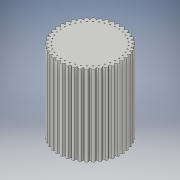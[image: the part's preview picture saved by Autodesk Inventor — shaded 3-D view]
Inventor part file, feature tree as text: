
AUTODESK INVENTOR PART (.ipt)
format: ipt  version: 2019.3 (Build 233278000, 278)  size: 697,856 bytes
history: native  units: mm
features: extrude x1
ambient origin geometry x8: Origin, YZ Plane, XZ Plane, XY Plane, X Axis, Y Axis, Z Axis, Center Point
bodies: Body1 (feature_tree)
feature tree (1):
  extrude  "Extrusion2"  Depth=5.047545mm
